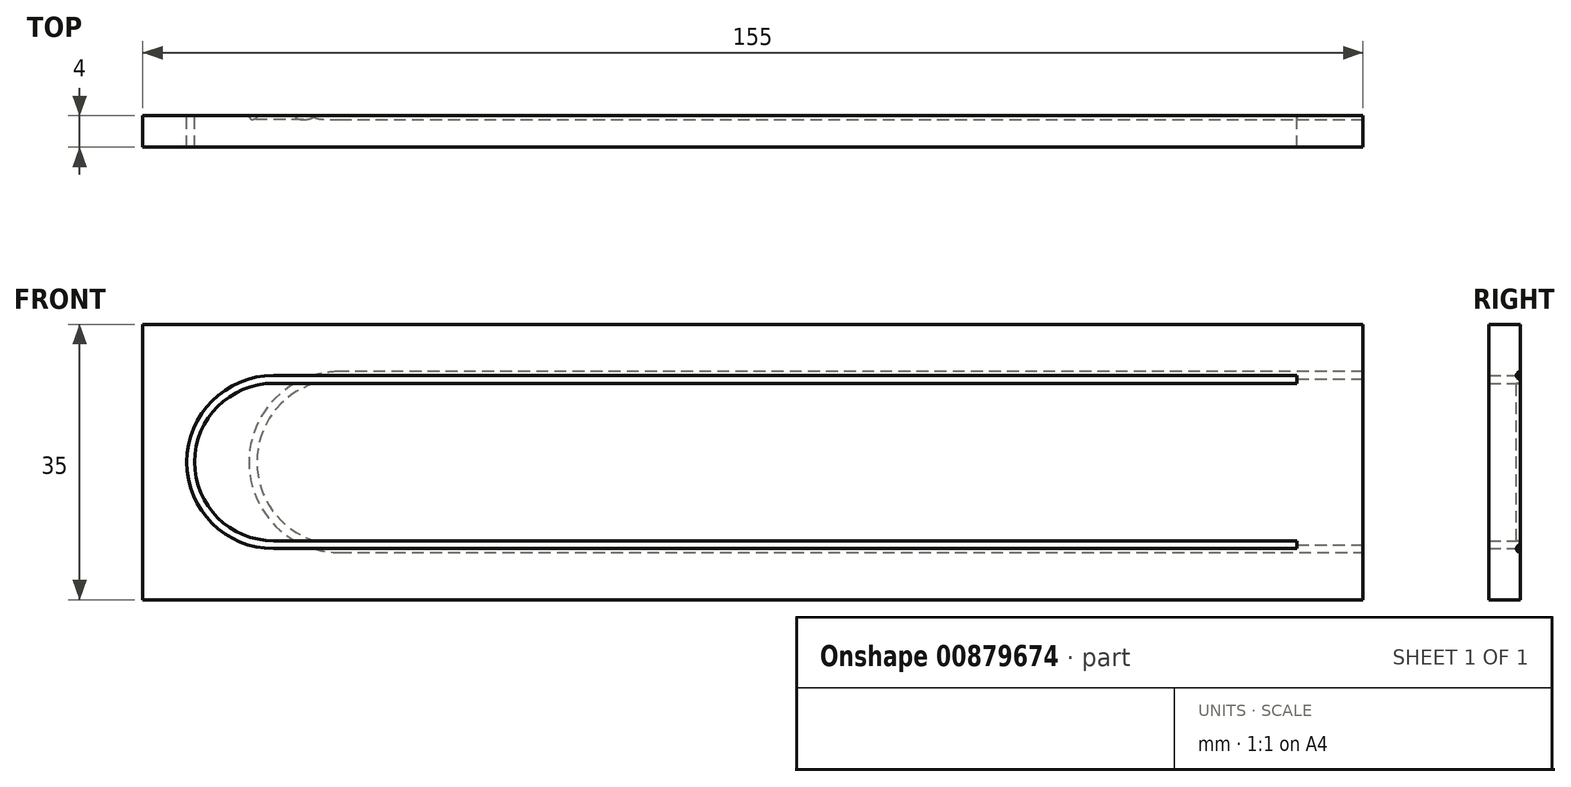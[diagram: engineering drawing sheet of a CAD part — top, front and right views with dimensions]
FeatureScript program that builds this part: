
annotation { "Feature Type Name" : "Feature", "Feature Type Description" : "" }
export const myFeature = defineFeature(function(context is Context, id is Id, definition is map)
    precondition{}
    {
        {
            assignVariable(context, id + "F0", {"name" : "PlyHeight", "anyValue" : 4 * mm});
        }
        {
            var Q0;
            Q0=qCreatedBy(makeId("Front.planeOp"),FACE);
            var sketch = newSketch(context, id + "F1", { "sketchPlane" : qUnion([Q0])});
            skArc(sketch, "E0", {"start": v(0, -11) * mm, "mid": v(-11, 0) * mm, "end": v(0, 11) * mm});
            skLineSegment(sketch, "E1", {"start": v(0, -11) * mm, "end": v(130, -11) * mm});
            skLineSegment(sketch, "E2", {"start": v(0, 11) * mm, "end": v(130, 11) * mm});
            skLineSegment(sketch, "E3.0", {"start": v(0, 10) * mm, "end": v(130, 10) * mm});
            skArc(sketch, "E3.1", {"start": v(0, -10) * mm, "mid": v(-10, 0) * mm, "end": v(0, 10) * mm});
            skLineSegment(sketch, "E3.2", {"start": v(0, -10) * mm, "end": v(130, -10) * mm});
            skLineSegment(sketch, "E4", {"start": v(130, -10) * mm, "end": v(130, -11) * mm});
            skLineSegment(sketch, "E5", {"start": v(130, 10) * mm, "end": v(130, 11) * mm});
            skSolve(sketch);
        }
        {
            var Q0;
            Q0=qCreatedBy(makeId("Right.planeOp"),FACE);
            var sketch = newSketch(context, id + "F2", { "sketchPlane" : qUnion([Q0])});
            skCircle(sketch, "E6", {"center": v(0, -11) * mm, "radius": 0.5 * mm});
            skSolve(sketch);
        }
        {
            var Q0;
            Q0=makeQuery(id+"F2.imprint","IMPRINT",FACE,{"disambiguationData":[TD([[makeQuery(id+"F2.imprint","IMPRINT",EDGE,{"derivedFrom":sQuery(id+"F2.wireOp",EDGE,"E6")}),1.0]])]});
            var Q1;
            Q1=sQuery(id+"F1.wireOp",EDGE,"E1");
            var Q2;
            Q2=sQuery(id+"F1.wireOp",EDGE,"E0");
            var Q3;
            Q3=sQuery(id+"F1.wireOp",EDGE,"E2");
            sweep(context, id + "F3", {"profiles" : qUnion([Q0]), "path" : qUnion([Q1, Q2, Q3])});
        }
        {
            var Q0;
            Q0=qCreatedBy(makeId("Front.planeOp"),FACE);
            var sketch = newSketch(context, id + "F4", { "sketchPlane" : qUnion([Q0])});
            skLineSegment(sketch, "E7.bottom", {"start": v(-25, -17.5) * mm, "end": v(130, -17.5) * mm});
            skLineSegment(sketch, "E7.top", {"start": v(-25, 17.5) * mm, "end": v(130, 17.5) * mm});
            skLineSegment(sketch, "E7.left", {"start": v(-25, -17.5) * mm, "end": v(-25, 17.5) * mm});
            skLineSegment(sketch, "E7.right", {"start": v(130, -17.5) * mm, "end": v(130, 17.5) * mm});
            skPoint(sketch, "E8", {"position": v(-25, 0) * mm});
            skLineSegment(sketch, "E9.0", {"start": v(-8.4, 11) * mm, "end": v(121.6, 11) * mm});
            skLineSegment(sketch, "E9.1", {"start": v(-8.4, 10) * mm, "end": v(121.6, 10) * mm});
            skArc(sketch, "E9.2", {"start": v(-8.4, -10) * mm, "mid": v(-18.4, 0) * mm, "end": v(-8.4, 10) * mm});
            skArc(sketch, "E9.3", {"start": v(-8.4, -11) * mm, "mid": v(-19.4, 0) * mm, "end": v(-8.4, 11) * mm});
            skLineSegment(sketch, "E9.4", {"start": v(-8.4, -10) * mm, "end": v(121.6, -10) * mm});
            skLineSegment(sketch, "E9.5", {"start": v(-8.4, -11) * mm, "end": v(121.6, -11) * mm});
            skLineSegment(sketch, "E10", {"start": v(121.6, -10) * mm, "end": v(121.6, -11) * mm});
            skLineSegment(sketch, "E11", {"start": v(121.6, 10) * mm, "end": v(121.6, 11) * mm});
            skSolve(sketch);
        }
        {
            var Q0;
            Q0=makeQuery(id+"F4.imprint","IMPRINT",FACE,{"disambiguationData":[TD([[makeQuery(id+"F4.imprint","IMPRINT",EDGE,{"derivedFrom":sQuery(id+"F4.wireOp",EDGE,"E7.bottom")}),1.0]])]});
            extrude(context, id + "F5", {"entities" : qUnion([Q0]), "depth" : getVariable(context, 'PlyHeight'), "offsetDistance" : 25 * mm});
        }
        {
            var Q0;
            Q0=makeQuery(id+"F3.opSweep","SWEPT_BODY",BODY,{"disambiguationData":[OSD([sQuery(id+"F1.wireOp",EDGE,"E2"),sQuery(id+"F2.wireOp",EDGE,"E6")])]});
            var Q1;
            Q1=makeQuery(id+"F5.opExtrude","SWEPT_BODY",BODY,{"disambiguationData":[OSD([sQuery(id+"F4.wireOp",EDGE,"E7.bottom"),sQuery(id+"F4.wireOp",EDGE,"E7.top"),sQuery(id+"F4.wireOp",EDGE,"E7.left"),sQuery(id+"F4.wireOp",EDGE,"E7.right")])]});
            booleanBodies(context, id + "F6", {"operationType" : BooleanOperationType.SUBTRACTION, "tools" : qUnion([Q0]), "targets" : qUnion([Q1])});
        }
    });
